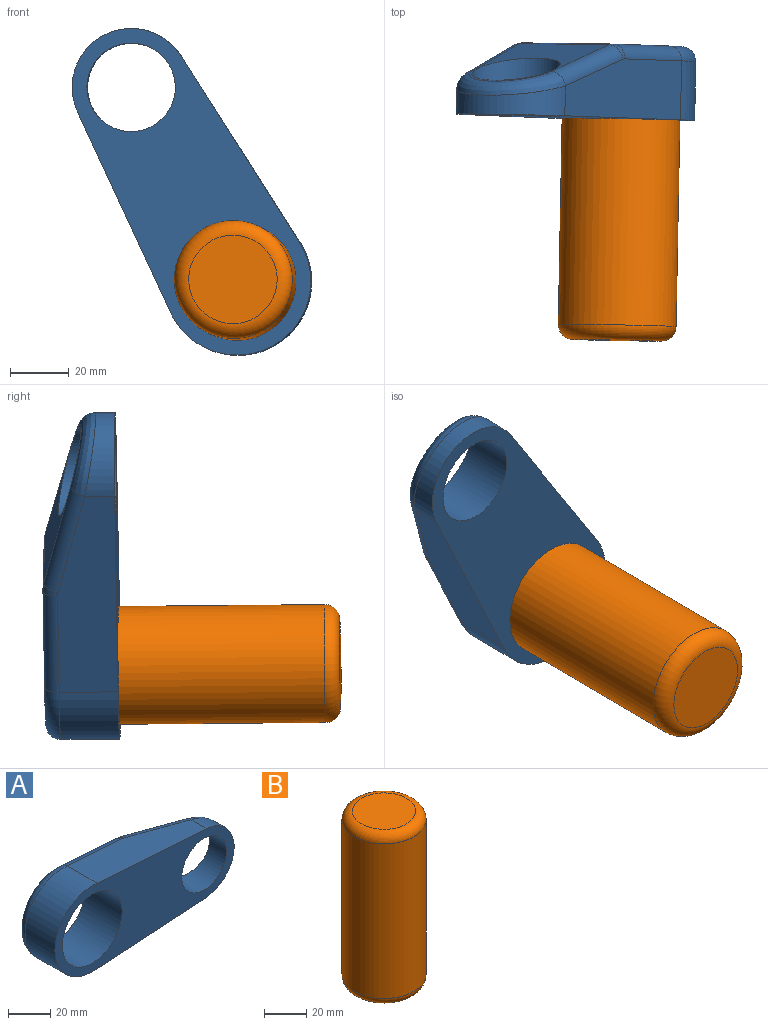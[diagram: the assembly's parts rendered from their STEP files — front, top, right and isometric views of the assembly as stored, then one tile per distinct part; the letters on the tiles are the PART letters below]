
ASSEMBLY  parts=2 mates=1
PART A: 18 faces, bbox 122.1x25x54.1 mm
  f0: plane 39.61x35.9mm, normal (0,1,0), area 819.5mm2, adj f6,f9,f13,f17
  f1: cylinder r=25mm len=50mm, axis (0,1,0), area 1702.8mm2, adj f2,f5,f7,f15
  f2: plane 73.03x20.01mm, normal (0.07,0,-1), area 1283.4mm2, adj f1,f3,f7,f14,f16,f17
  f3: cylinder r=20mm len=39.91mm, axis (0,1,0), area 468.3mm2, adj f2,f5,f7,f12
  f4: cylinder r=15mm len=30mm, axis (0,1,0), area 1472.3mm2, adj f7,f8
  f5: plane 73.03x20.01mm, normal (0.07,0,1), area 1283.4mm2, adj f1,f3,f7,f10,f11,f13
  f6: cylinder r=20mm len=40mm, axis (0,1,0), area 3141.6mm2, adj f0,f7,f15
  f7: plane 120x50mm, normal (0,-1,0), area 3025.1mm2, adj f1,f2,f3,f4,f5,f6
  f8: plane 50.02x34.69mm, normal (0.26,0.97,0), area 808.2mm2, adj f4,f9,f10,f12,f14
  f9: cylinder r=10mm len=34.87mm, axis (0,0,1), area 91.1mm2, adj f0,f8,f11,f16
  f10: cylinder r=5mm len=37.01mm, axis (-0.96,0.26,0.06), area 290.2mm2, adj f5,f8,f11,f12
  f11: bspline ~5.17x5.07mm, area 16.7mm2, adj f5,f9,f10,f13
  f12: bspline ~39.91x18.67mm, area 383.4mm2, adj f3,f8,f10,f14
  f13: cylinder r=5mm len=36.23mm, axis (-1,0,0.07), area 281.9mm2, adj f0,f5,f11,f15
  f14: cylinder r=5mm len=37.01mm, axis (0.96,-0.26,0.06), area 290.2mm2, adj f2,f8,f12,f16
  f15: torus R=20mm, axis (0,-1,0), area 621mm2, adj f1,f6,f13,f17
  f16: bspline ~6.09x5.45mm, area 16.7mm2, adj f2,f9,f14,f17
  f17: cylinder r=5mm len=36.23mm, axis (1,0,0.07), area 281.9mm2, adj f0,f2,f15,f16
PART B: 5 faces, bbox 43.3x43.3x100 mm
  f0: cylinder r=20mm len=90mm, axis (0,0,-1), area 11309.7mm2, adj f3,f4
  f1: plane 30x30mm, normal (0,0,1), area 706.9mm2, adj f4
  f2: plane 30x30mm, normal (0,0,-1), area 706.9mm2, adj f3
  f3: torus R=15mm, axis (0,0,1), area 897.3mm2, adj f0,f2
  f4: torus R=15mm, axis (0,0,1), area 897.3mm2, adj f0,f1
PLACE A rot(axis=(-0.01,-1,0),118.7deg) t=(20.8,-154.66,95)mm
PLACE B rot(axis=(0.18,0.69,-0.7),160.5deg) t=(1.02,-154.74,43.22)mm
MATE fastened A.f6 <-> B.f0  axis (0.02,1,-0.01) through (20.8,-154.66,95)mm
